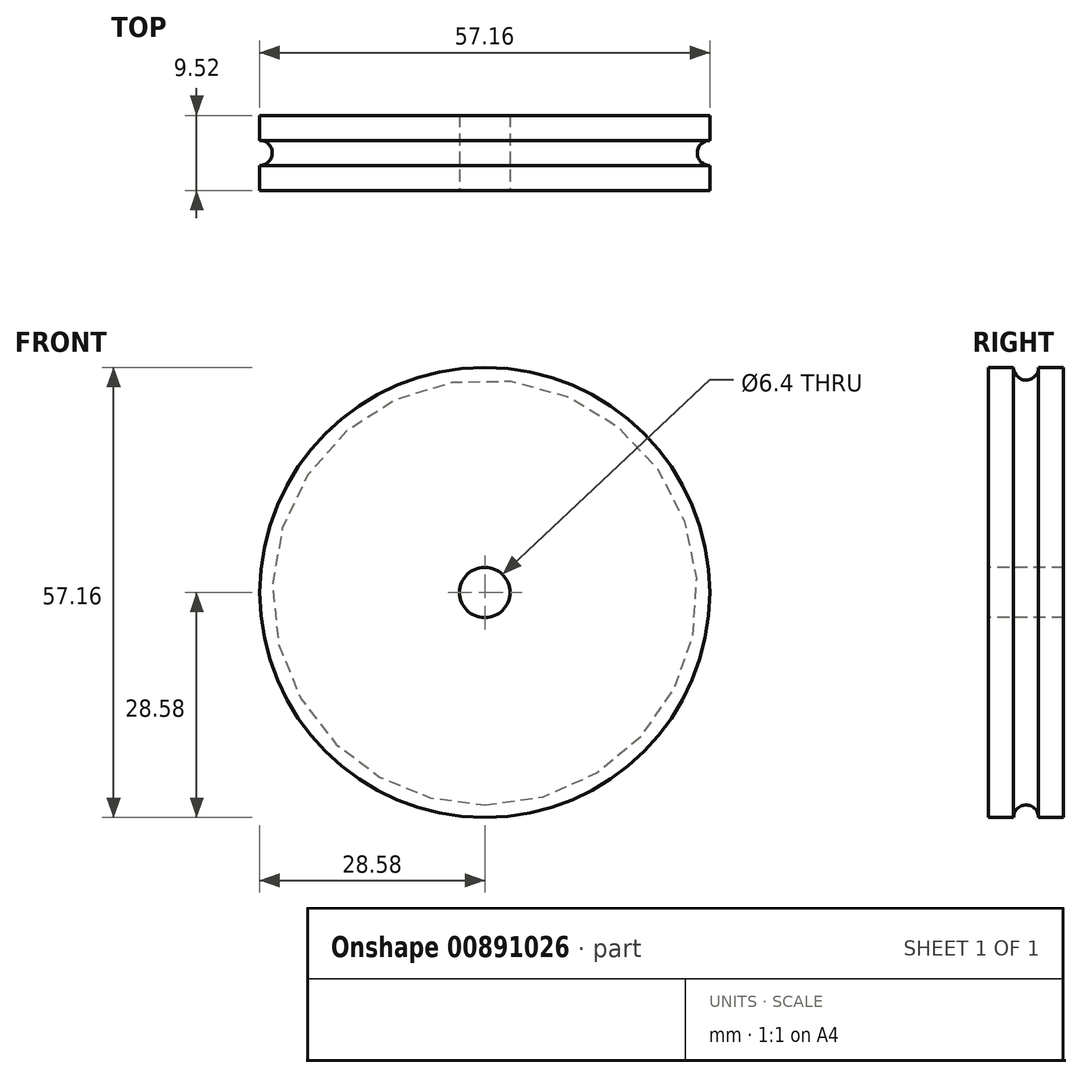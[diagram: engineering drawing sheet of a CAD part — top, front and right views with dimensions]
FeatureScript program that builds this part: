
annotation { "Feature Type Name" : "Feature", "Feature Type Description" : "" }
export const myFeature = defineFeature(function(context is Context, id is Id, definition is map)
    precondition{}
    {
        {
            var Q0;
            Q0=qCreatedBy(makeId("Right.planeOp"),FACE);
            var sketch = newSketch(context, id + "F0", { "sketchPlane" : qUnion([Q0])});
            skLineSegment(sketch, "E0", {"start": v(-4.76, 0) * mm, "end": v(-4.76, 28.58) * mm});
            skLineSegment(sketch, "E1", {"start": v(4.76, 0) * mm, "end": v(4.76, 28.58) * mm});
            skLineSegment(sketch, "E2", {"start": v(-4.76, 28.58) * mm, "end": v(-1.59, 28.58) * mm});
            skLineSegment(sketch, "E3", {"start": v(4.76, 28.58) * mm, "end": v(1.59, 28.58) * mm});
            skArc(sketch, "E4", {"start": v(-1.59, 28.58) * mm, "mid": v(0, 26.99) * mm, "end": v(1.59, 28.58) * mm});
            skLineSegment(sketch, "E5", {"start": v(0, 0) * mm, "end": v(-4.76, 0) * mm});
            skLineSegment(sketch, "E6", {"start": v(0, 0) * mm, "end": v(4.76, 0) * mm});
            skSolve(sketch);
        }
        {
            var Q0;
            Q0=makeQuery(id+"F0.imprint","IMPRINT",FACE,{"disambiguationData":[TD([[makeQuery(id+"F0.imprint","IMPRINT",EDGE,{"derivedFrom":sQuery(id+"F0.wireOp",EDGE,"E0")}),-1.0]])]});
            var Q1;
            Q1=sQuery(id+"F0.wireOp",EDGE,"E6");
            revolve(context, id + "F1", {"surfaceOperationType" : NewSurfaceOperationType.NEW, "entities" : qUnion([Q0]), "axis" : qUnion([Q1]), "revolveType" : RevolveType.FULL});
        }
        {
            var Q0;
            Q0=makeQuery(id+"F1.opRevolve","SWEPT_FACE",FACE,{"disambiguationData":[OSD([sQuery(id+"F0.wireOp",EDGE,"E0")])]});
            var sketch = newSketch(context, id + "F2", { "sketchPlane" : qUnion([Q0])});
            skPoint(sketch, "E7", {"position": v(0, 0) * mm});
            skSolve(sketch);
        }
        {
            var Q0;
            Q0=sQuery(id+"F2.wireOp",VERTEX,"E7");
            var Q1;
            Q1=makeQuery(id+"F1.opRevolve","SWEPT_BODY",BODY,{"disambiguationData":[OSD([sQuery(id+"F0.wireOp",EDGE,"E0"),sQuery(id+"F0.wireOp",EDGE,"E1"),sQuery(id+"F0.wireOp",EDGE,"E2"),sQuery(id+"F0.wireOp",EDGE,"E3"),sQuery(id+"F0.wireOp",EDGE,"E4"),sQuery(id+"F0.wireOp",EDGE,"E5"),sQuery(id+"F0.wireOp",EDGE,"E6")])]});
            hole(context, id + "F3", {"style" : HoleStyle.SIMPLE, "endStyle" : HoleEndStyle.THROUGH, "holeDiameter" : 6.4 * mm, "majorDiameter" : 6.35 * mm, "isTappedThrough" : true, "tappedDepth" : 12.7 * mm, "tapClearance" : 3, "locations" : qUnion([Q0]), "scope" : qUnion([Q1])});
        }
    });
